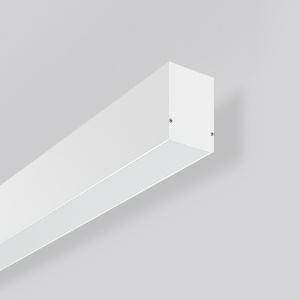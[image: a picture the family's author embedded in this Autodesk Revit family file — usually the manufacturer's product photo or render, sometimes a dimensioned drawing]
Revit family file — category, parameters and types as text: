
# Revit family: less_is_more_50_312611_002_1_28fb
name_source: partatom
category: Lighting Fixtures
units: mm (PartAtom-declared; Revit-internal decimal feet)

## family parameters
Cut with Voids When Loaded = No
Host = Face
Light Source = No
Part Type = Normal
Room Calculation Point = No
Round Connector Dimension = Use Diameter
Shared = No

## types (1)
- LESS IS MORE 50 (1 x LED Modul 840, 2300 lm, 4000)
    Apparent Load = 18 VA
    CIE Flux Codes = 48 80 96 100 100
    Color Rendering = 80
    Color Temperature = 4000
    Default Elevation = 1800 mm
    Description = Series: LESS IS MORE 50
Linear wall luminaires. Housing: extruded aluminium profile, powder-coated. End cap aluminium powder-coated. Diffuser made of non-yellowing plastic (PMMA), opal. Direct light emission. Suitable for Wall (surface). LED unit with integrated converter interchangeable and removable. Suitable for through-wiring. With sensors or as a safety luminaire on request. 
Colour: traffic white, matt (RAL 9016)
Length: 1687 mm
Width: 67 mm
Height: 75 mm
Lamp: LED
Socket: without socket
Colour temperature: 4000K
Colour rendering index (CRI): 80
System power: 18 W
Rated luminous flux: 2300 lm
Luminous efficiency: 128 lm/W
Control gear: Regulated power supply
Protection class: I
Type of protection: IP 20
    Height = 75 mm
    Lamp = 1 x LED Modul 840
    Lamp Light Flux = 2300 lm
    Lamp count = 1
    Length = 1687 mm
    Lifetime = 50000 h
    Luminous efficacy = 128 lm/W
    Manufacturer = RZB
    ModVariant = No
    Model = 312611.002.1
    Mounting Place = Wall
    Mounting Type = Surface mounted
    Number of Poles = 1
    OnlyDefault = Yes
    Power Factor = 1
    Product Name = LESS IS MORE 50
    Product group = Surface mounted LED linear luminaires
    ProductGroupID = 2007
    Protection Class = Protection class I
    Protection Degree = IP 20
    RLX_Detail_Level = 1
    RLX_Emergency_Light_Flux = 0 lm
    RLX_Emergency_Type = 0
    RLX_Emergency_Type_DB = No
    RlxData = <blob elided: 35205 chars, md5=1a50d3c7>
    Socket = socket
    Standby Power = 0 W
    System Light Flux = 2300 lm
    System Power = 18 W
    Type Comments = Product without accessories
    Type Image = 312606.002.jpg
    URL = http://relux.com
    VarID = ---
    Voltage = 0 V
    Weight = 0.00 kg
    Width = 67 mm

## geometry (parser evidence)
native form markers: Blend x4, Sweep x9
no freeform markers — native parametric forms only
